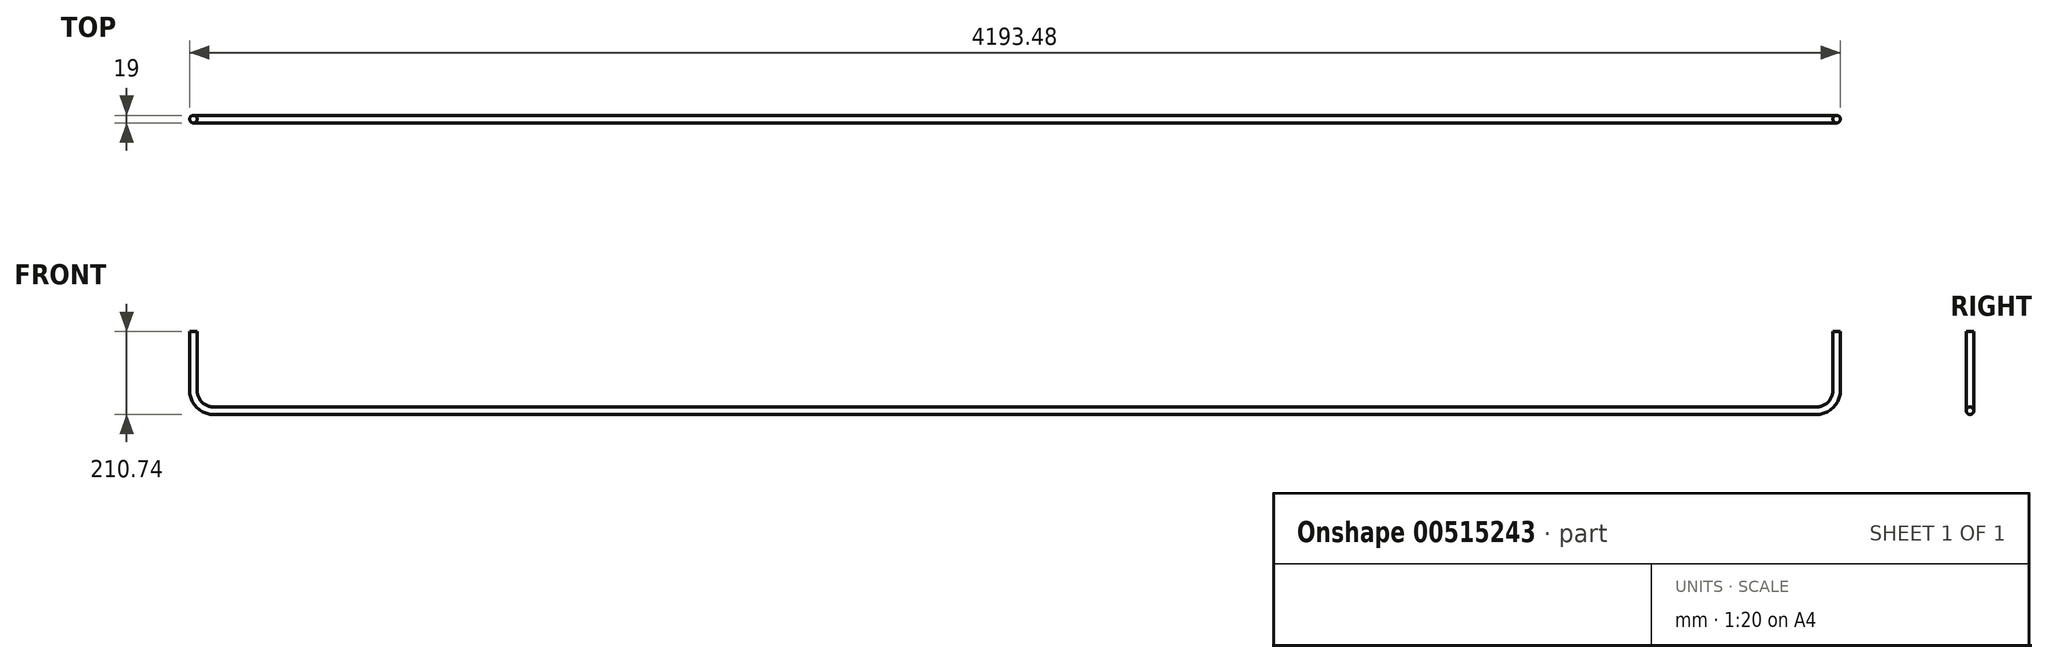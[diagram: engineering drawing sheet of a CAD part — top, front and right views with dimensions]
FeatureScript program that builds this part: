
annotation { "Feature Type Name" : "Feature", "Feature Type Description" : "" }
export const myFeature = defineFeature(function(context is Context, id is Id, definition is map)
    precondition{}
    {
        {
            var Q0;
            Q0=qCreatedBy(makeId("Front.planeOp"),FACE);
            var sketch = newSketch(context, id + "F0", { "sketchPlane" : qUnion([Q0])});
            skLineSegment(sketch, "E0", {"start": v(-2086, 200) * mm, "end": v(-2086, 50) * mm});
            skLineSegment(sketch, "E1", {"start": v(-2036, 0) * mm, "end": v(2036, 0) * mm});
            skLineSegment(sketch, "E2", {"start": v(2086, 50) * mm, "end": v(2086, 200) * mm});
            skPoint(sketch, "E3.visualSharp", {"position": v(-2086, 0) * mm});
            skArc(sketch, "E3.filletArc", {"start": v(-2086, 50) * mm, "mid": v(-2071.36, 14.64) * mm, "end": v(-2036, 0) * mm});
            skPoint(sketch, "E4.visualSharp", {"position": v(2086, 0) * mm});
            skArc(sketch, "E4.filletArc", {"start": v(2036, 0) * mm, "mid": v(2071.36, 14.64) * mm, "end": v(2086, 50) * mm});
            skSolve(sketch);
        }
        {
            var Q0;
            Q0=sQuery(id+"F0.wireOp",VERTEX,"E0.start");
            var Q1;
            Q1=qCreatedBy(makeId("Top.planeOp"),FACE);
            cPlane(context, id + "F1", {"entities" : qUnion([Q0, Q1]), "cplaneType" : CPlaneType.PLANE_POINT, "offset" : 25 * mm, "width" : 150 * mm, "height" : 150 * mm});
        }
        {
            var Q0;
            Q0=qCreatedBy(id+"F1.planeOp",FACE);
            var sketch = newSketch(context, id + "F2", { "sketchPlane" : qUnion([Q0])});
            skCircle(sketch, "E5", {"center": v(-2087.24, 0) * mm, "radius": 9.5 * mm});
            skSolve(sketch);
        }
        {
            var Q0;
            Q0=makeQuery(id+"F2.imprint","IMPRINT",FACE,{"disambiguationData":[TD([[makeQuery(id+"F2.imprint","IMPRINT",EDGE,{"derivedFrom":sQuery(id+"F2.wireOp",EDGE,"E5")}),1.0]])]});
            var Q1;
            Q1=sQuery(id+"F0.wireOp",EDGE,"E0");
            var Q2;
            Q2=sQuery(id+"F0.wireOp",EDGE,"E3.filletArc");
            var Q3;
            Q3=sQuery(id+"F0.wireOp",EDGE,"E1");
            var Q4;
            Q4=sQuery(id+"F0.wireOp",EDGE,"E4.filletArc");
            var Q5;
            Q5=sQuery(id+"F0.wireOp",EDGE,"E2");
            sweep(context, id + "F3", {"profiles" : qUnion([Q0]), "path" : qUnion([Q1, Q2, Q3, Q4, Q5])});
        }
    });
